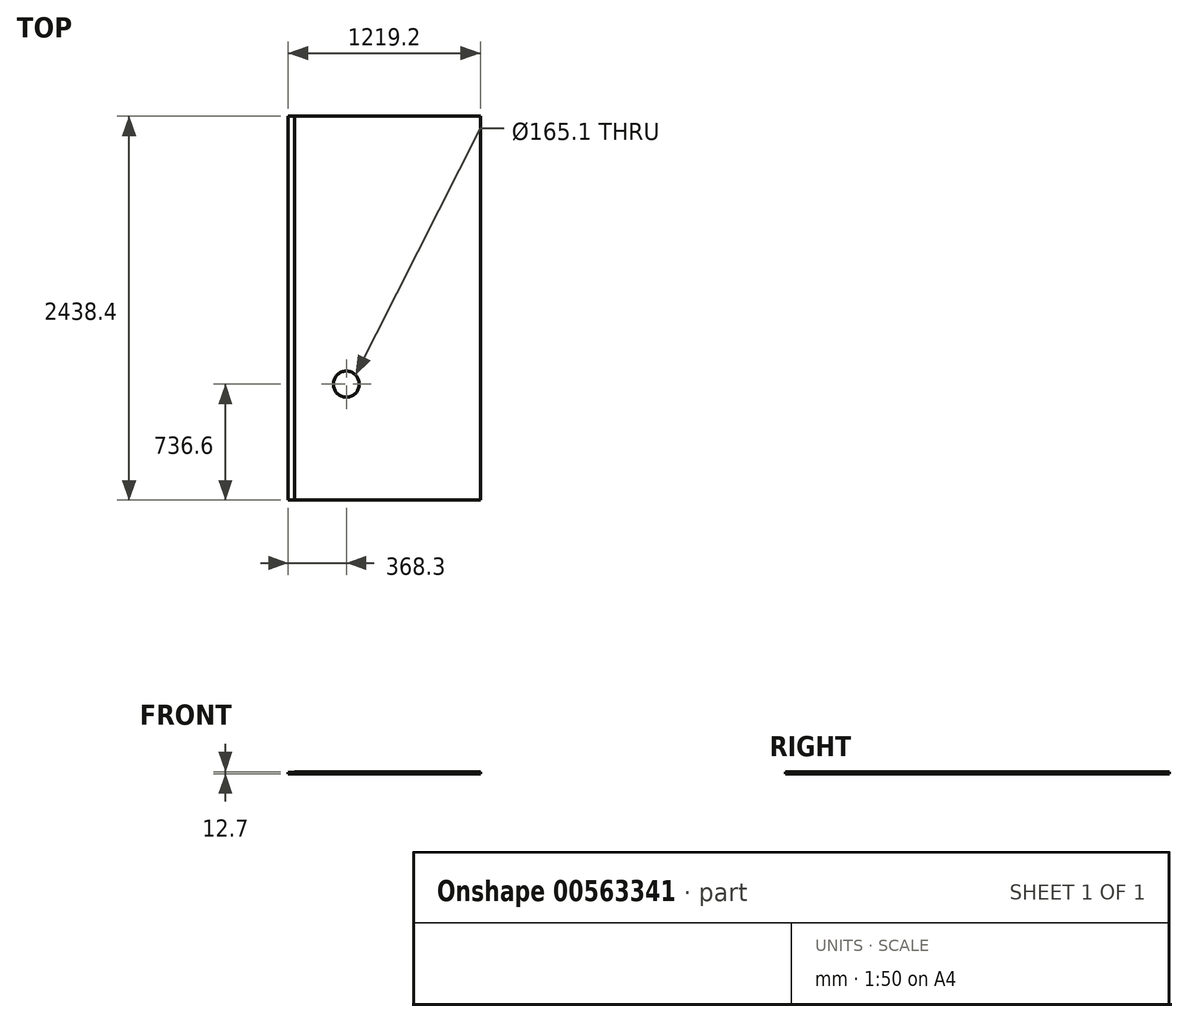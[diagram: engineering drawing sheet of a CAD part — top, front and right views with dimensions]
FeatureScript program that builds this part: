
annotation { "Feature Type Name" : "Feature", "Feature Type Description" : "" }
export const myFeature = defineFeature(function(context is Context, id is Id, definition is map)
    precondition{}
    {
        {
            var Q0;
            Q0=qCreatedBy(makeId("Front.planeOp"),FACE);
            var sketch = newSketch(context, id + "F0", { "sketchPlane" : qUnion([Q0])});
            skLineSegment(sketch, "E0.bottom", {"start": v(-571.5, 6.35) * mm, "end": v(609.6, 6.35) * mm});
            skLineSegment(sketch, "E0.top", {"start": v(-609.6, -6.35) * mm, "end": v(609.6, -6.35) * mm});
            skLineSegment(sketch, "E0.right", {"start": v(609.6, 6.35) * mm, "end": v(609.6, -6.35) * mm});
            skPoint(sketch, "E0.middle", {"position": v(0, 0) * mm});
            skPoint(sketch, "E1.orphan", {"position": v(-609.6, 6.35) * mm});
            skLineSegment(sketch, "E2", {"start": v(-609.6, -6.35) * mm, "end": v(-609.6, 3.17) * mm});
            skLineSegment(sketch, "E3", {"start": v(-609.6, 3.17) * mm, "end": v(-571.5, 6.35) * mm});
            skSolve(sketch);
        }
        {
            var Q0;
            Q0 = qSketchRegion(id + "F0", true);
            extrude(context, id + "F1", {"entities" : qUnion([Q0]), "depth" : 2438.4 * mm, "offsetDistance" : 25.4 * mm});
        }
        {
            var Q0;
            Q0=makeQuery(id+"F1.opExtrude","SWEPT_FACE",FACE,{"disambiguationData":[OSD([sQuery(id+"F0.wireOp",EDGE,"E0.top")])]});
            var sketch = newSketch(context, id + "F2", { "sketchPlane" : qUnion([Q0])});
            skLineSegment(sketch, "E4", {"start": v(-609.6, 1701.8) * mm, "end": v(609.6, 1701.8) * mm, "construction": true});
            skLineSegment(sketch, "E5", {"start": v(-241.3, 2438.4) * mm, "end": v(-241.3, 0) * mm, "construction": true});
            skCircle(sketch, "E6", {"center": v(-241.3, 1701.8) * mm, "radius": 82.55 * mm});
            skSolve(sketch);
        }
        {
            var Q0;
            Q0=makeQuery(id+"F2.imprint","IMPRINT",FACE,{"disambiguationData":[TD([[makeQuery(id+"F2.imprint","IMPRINT",EDGE,{"derivedFrom":sQuery(id+"F2.wireOp",EDGE,"E6")}),1.0]])]});
            extrude(context, id + "F3", {"entities" : qUnion([Q0]), "operationType" : NewBodyOperationType.REMOVE, "oppositeDirection" : true, "depth" : 25.4 * mm, "offsetDistance" : 25.4 * mm});
        }
    });
